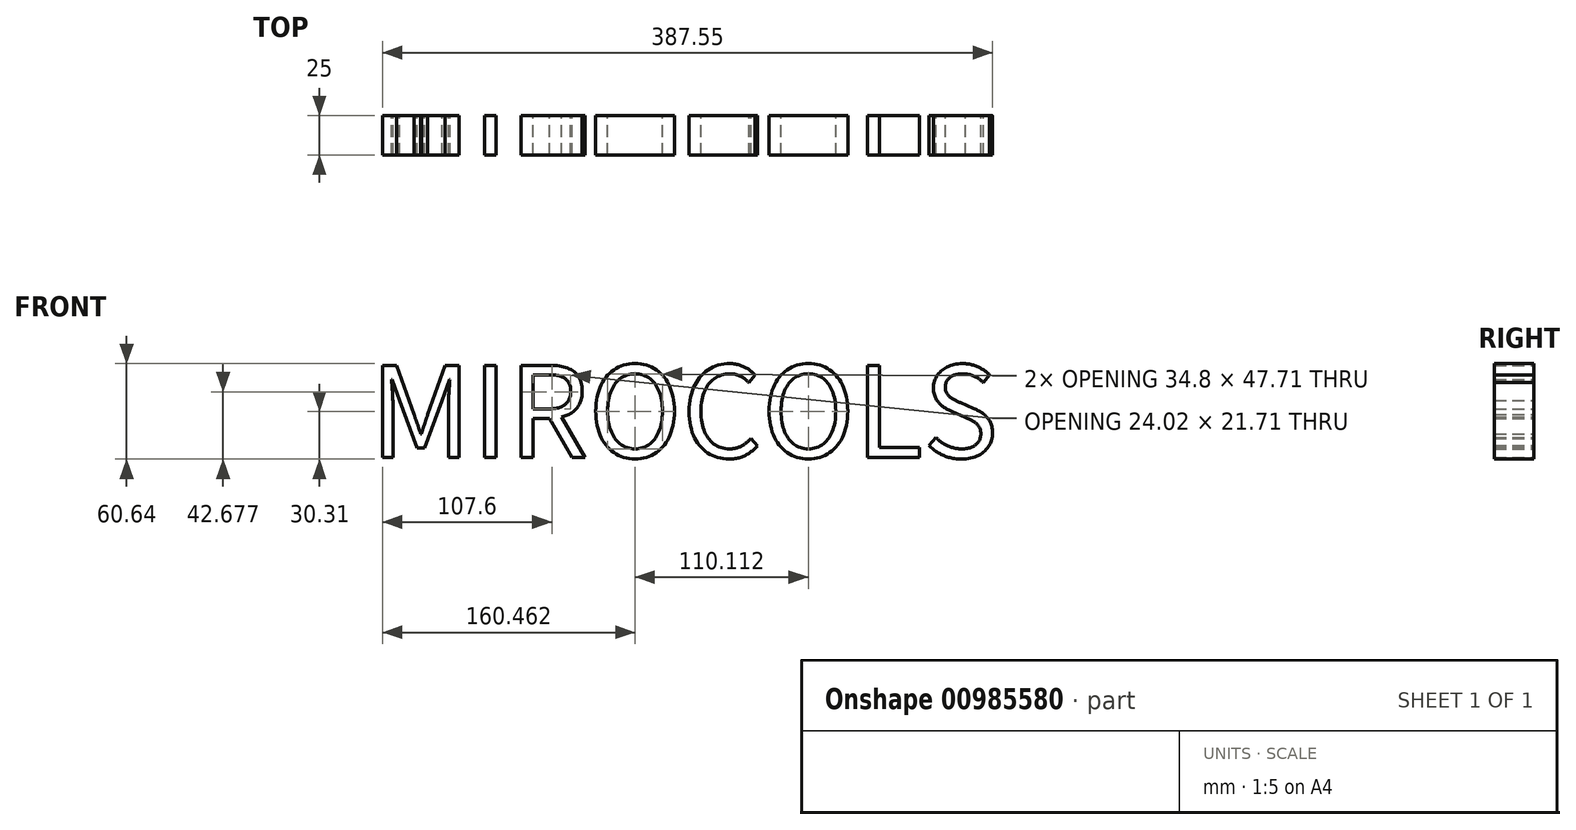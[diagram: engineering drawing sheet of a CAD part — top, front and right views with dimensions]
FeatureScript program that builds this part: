
annotation { "Feature Type Name" : "Feature", "Feature Type Description" : "" }
export const myFeature = defineFeature(function(context is Context, id is Id, definition is map)
    precondition{}
    {
        {
            var Q0;
            Q0=qCreatedBy(makeId("Front.planeOp"),FACE);
            var sketch = newSketch(context, id + "F0", { "sketchPlane" : qUnion([Q0])});
            skText(sketch, "E0", { "text": "MIROCOLS", "fontName": "NotoSansCJKsc-Regular.otf"});
            const initialGuessF0  = {"E0": [-0.2, -0.05745, 1, 0, 0.05745]};
            skSetInitialGuess(sketch, initialGuessF0);
            skSolve(sketch);
        }
        {
            var Q0;
            Q0 = qSketchRegion(id + "F0", true);
            extrude(context, id + "F1", {"entities" : qUnion([Q0]), "depth" : 25 * mm, "offsetDistance" : 25 * mm});
        }
    });
